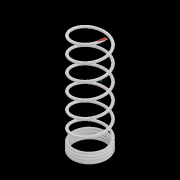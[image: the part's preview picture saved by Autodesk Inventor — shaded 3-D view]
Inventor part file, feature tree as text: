
AUTODESK INVENTOR PART (.ipt)
format: ipt  version: 2020 (Build 240168000, 168)  size: 503,808 bytes
history: native  units: mm
features: sketch x10, plane x9, other x8, extrude x4, helix x2, pattern_linear x1
ambient origin geometry x8: Origin, YZ Plane, XZ Plane, XY Plane, X Axis, Y Axis, Z Axis, Center Point
bodies: Body1 (feature_tree)
feature tree (34):
  helix  "螺旋3"  [1 undecoded]
  helix  "螺旋4"  [1 undecoded]
  extrude  "擠出2"  Depth=500.0mm
  plane  "工作平面1"
  sketch  "草圖13"
  plane  "工作平面2"
  plane  "工作平面3"
  sketch  "草圖14"
  plane  "工作平面5"
  pattern_linear  "矩形陣列1"  Spacing1=10.0mm  [1 undecoded]
  sketch  "草圖15"
  sketch  "草圖6"
  extrude  "擠出3"  Depth=40.0mm
  extrude  "擠出4"  Depth=10.0mm
  extrude  "擠出5"  TaperAngle=0.0deg  [1 undecoded]
  sketch  "草圖1"
  sketch  "草圖4"
  sketch  "草圖5"
  sketch  "草圖7"
  other  "實體3"
  sketch  "草圖8"
  sketch  "草圖9"
  plane  "工作平面4"
  plane  "工作平面6"
  plane  "工作平面7"
  plane  "工作平面8"
  plane  "工作平面9"
  other  "投影切割邊3"
  other  "投影切割邊4"
  other  "投影切割邊5"
  other  "投影切割邊6"
  other  "投影切割邊8"
  other  "投影切割邊9"
  other  "投影切割邊10"
note: 4 required parameter values undecoded (feature->parameter linkage not recoverable at this tier; creation-order binding heuristic only, values carry confidence <= 0.55)
